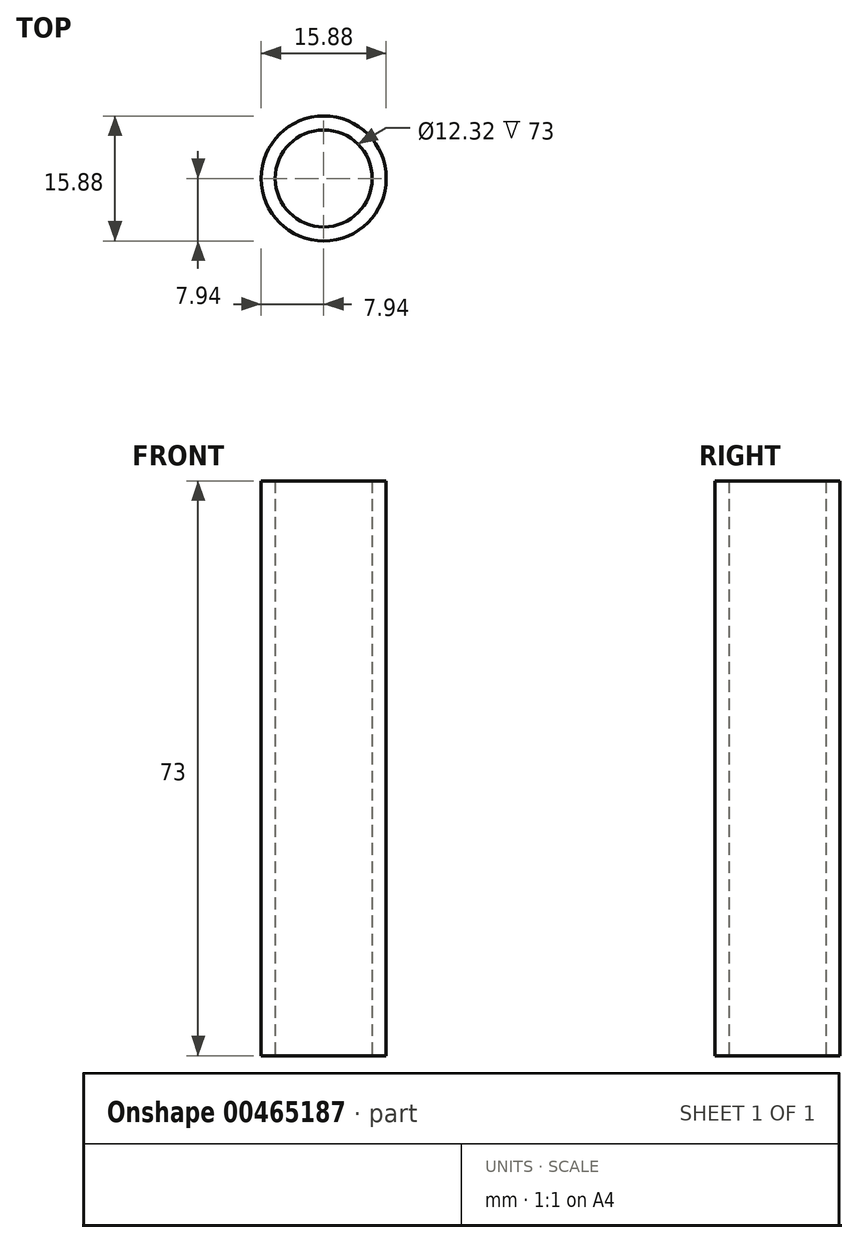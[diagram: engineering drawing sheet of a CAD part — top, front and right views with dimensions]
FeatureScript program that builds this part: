
annotation { "Feature Type Name" : "Feature", "Feature Type Description" : "" }
export const myFeature = defineFeature(function(context is Context, id is Id, definition is map)
    precondition{}
    {
        {
            var Q0;
            Q0=qCreatedBy(makeId("Top.planeOp"),FACE);
            var sketch = newSketch(context, id + "F0", { "sketchPlane" : qUnion([Q0])});
            skCircle(sketch, "E0", {"center": v(0, 0) * mm, "radius": 6.16 * mm});
            skCircle(sketch, "E1", {"center": v(0, 0) * mm, "radius": 7.94 * mm});
            skSolve(sketch);
        }
        {
            var Q0;
            Q0=makeQuery(id+"F0.imprint","IMPRINT",FACE,{"disambiguationData":[TD([[makeQuery(id+"F0.imprint","IMPRINT",EDGE,{"derivedFrom":sQuery(id+"F0.wireOp",EDGE,"E0")}),-1.0]])]});
            extrude(context, id + "F1", {"entities" : qUnion([Q0]), "depth" : 73 * mm, "offsetDistance" : 25.4 * mm});
        }
    });
